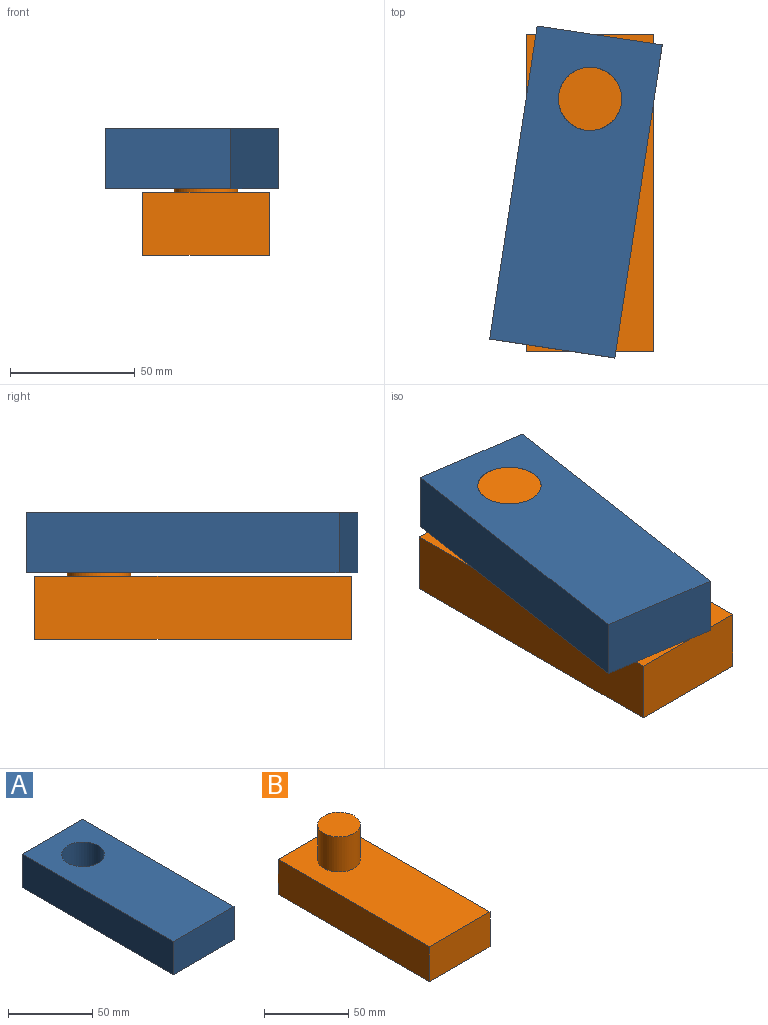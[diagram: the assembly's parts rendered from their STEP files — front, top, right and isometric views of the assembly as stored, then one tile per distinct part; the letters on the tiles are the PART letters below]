
ASSEMBLY  parts=2 mates=1
PART A: 7 faces, bbox 50.8x127x24.1 mm
  f0: plane 50.8x24.13mm, normal (0,1,0), area 1225.8mm2, adj f1,f4,f5,f6
  f1: plane 127x24.13mm, normal (-1,0,0), area 3064.5mm2, adj f0,f2,f5,f6
  f2: plane 50.8x24.13mm, normal (0,-1,0), area 1225.8mm2, adj f1,f4,f5,f6
  f3: cylinder r=12.7mm len=25.4mm, axis (0,0,-1), area 1925.5mm2, adj f5,f6
  f4: plane 127x24.13mm, normal (1,0,0), area 3064.5mm2, adj f0,f2,f5,f6
  f5: plane 127x50.8mm, normal (0,0,1), area 5944.9mm2, adj f0,f1,f2,f3,f4
  f6: plane 127x50.8mm, normal (0,0,-1), area 5944.9mm2, adj f0,f1,f2,f3,f4
PART B: 8 faces, bbox 50.8x127x50.8 mm
  f0: plane 50.8x25.4mm, normal (0,1,0), area 1290.3mm2, adj f1,f3,f4,f5
  f1: plane 127x25.4mm, normal (-1,0,0), area 3225.8mm2, adj f0,f2,f4,f5
  f2: plane 50.8x25.4mm, normal (0,-1,0), area 1290.3mm2, adj f1,f3,f4,f5
  f3: plane 127x25.4mm, normal (1,0,0), area 3225.8mm2, adj f0,f2,f4,f5
  f4: plane 127x50.8mm, normal (0,0,1), area 5944.9mm2, adj f0,f1,f2,f3,f6
  f5: plane 127x50.8mm, normal (0,0,-1), area 6451.6mm2, adj f0,f1,f2,f3
  f6: cylinder r=12.7mm len=25.4mm, axis (0,0,-1), area 2026.8mm2, adj f4,f7
  f7: plane 25.4x25.4mm, normal (0,0,1), area 506.7mm2, adj f6
PLACE A rot(axis=(0,0,-1),8.6deg) t=(-29.67,2.46,-11.23)mm
PLACE B t=(-24.02,2.03,-12.5)mm fixed
MATE revolute A.f3 <-> B.f6  axis (0,0,1) through (-24.02,39.8,38.3)mm
